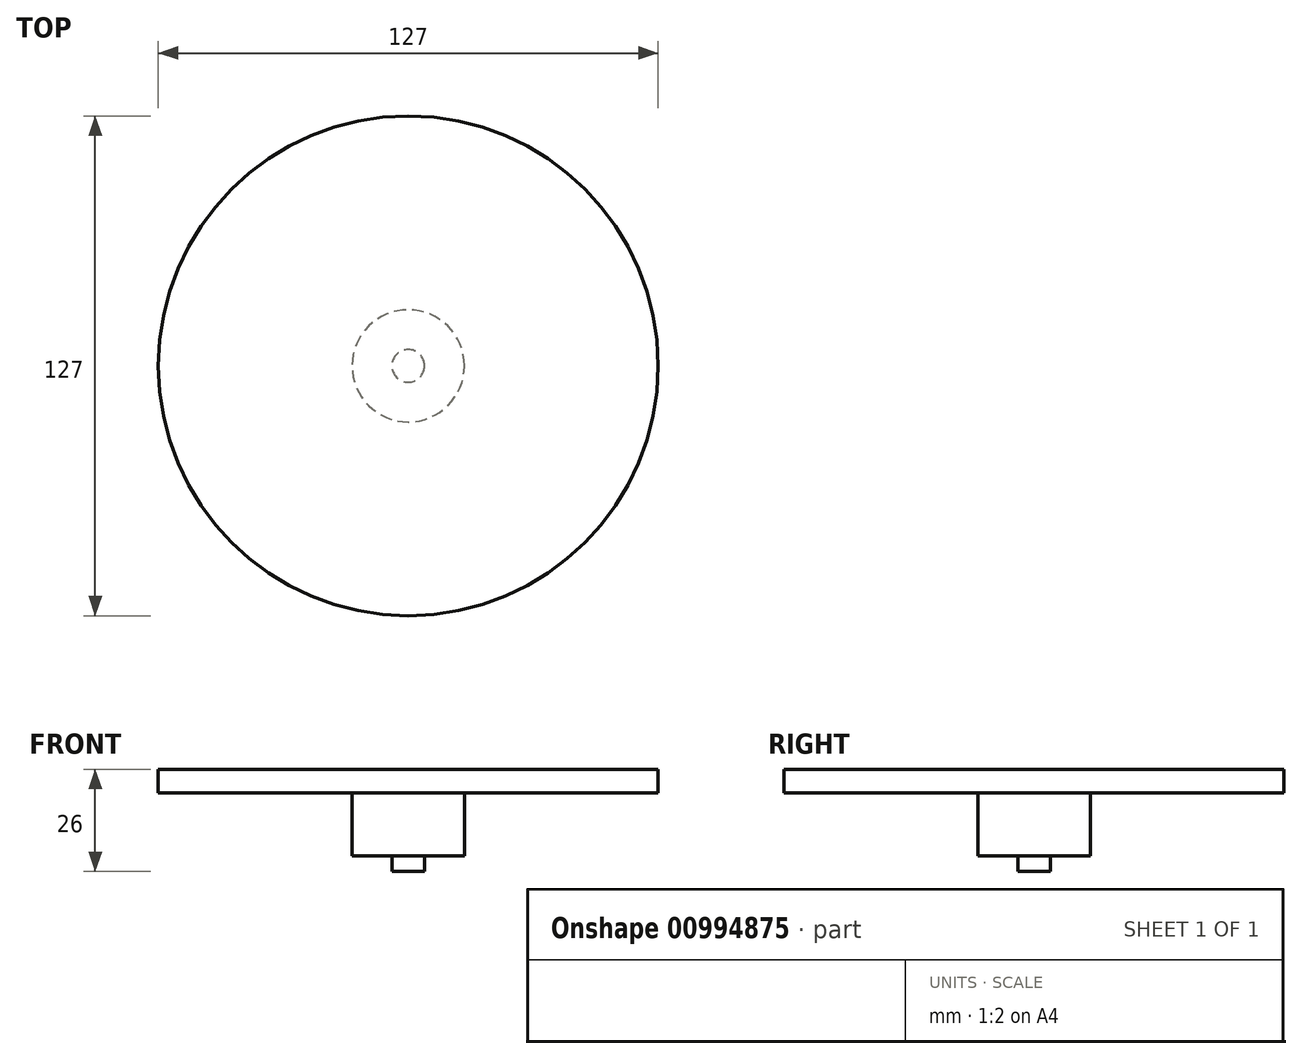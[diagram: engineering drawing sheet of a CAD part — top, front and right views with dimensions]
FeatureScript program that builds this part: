
annotation { "Feature Type Name" : "Feature", "Feature Type Description" : "" }
export const myFeature = defineFeature(function(context is Context, id is Id, definition is map)
    precondition{}
    {
        {
            var Q0;
            Q0=qCreatedBy(makeId("Top.planeOp"),FACE);
            var sketch = newSketch(context, id + "F0", { "sketchPlane" : qUnion([Q0])});
            skCircle(sketch, "E0", {"center": v(0, 0) * mm, "radius": 14.25 * mm});
            skCircle(sketch, "E1", {"center": v(0, 0) * mm, "radius": 2.5 * mm});
            skSolve(sketch);
        }
        {
            var Q0;
            Q0=makeQuery(id+"F0.imprint","IMPRINT",FACE,{"disambiguationData":[TD([[makeQuery(id+"F0.imprint","IMPRINT",EDGE,{"derivedFrom":sQuery(id+"F0.wireOp",EDGE,"E0")}),1.0]])]});
            extrude(context, id + "F1", {"entities" : qUnion([Q0]), "depth" : 16 * mm, "offsetDistance" : 25 * mm});
        }
        {
            var Q0;
            Q0=makeQuery(id+"F0.imprint","IMPRINT",FACE,{"disambiguationData":[TD([[makeQuery(id+"F0.imprint","IMPRINT",EDGE,{"derivedFrom":sQuery(id+"F0.wireOp",EDGE,"E1")}),1.0]])]});
            extrude(context, id + "F2", {"entities" : qUnion([Q0]), "operationType" : NewBodyOperationType.ADD, "depth" : 19 * mm, "offsetDistance" : 25 * mm});
        }
        {
            var Q0;
            Q0=makeQuery(id+"F1.opExtrude","CAP_FACE",FACE,{"disambiguationData":[OSD([sQuery(id+"F0.wireOp",EDGE,"E0"),sQuery(id+"F0.wireOp",EDGE,"E1")])],"isStart":false});
            var sketch = newSketch(context, id + "F3", { "sketchPlane" : qUnion([Q0])});
            skCircle(sketch, "E2", {"center": v(0, 0) * mm, "radius": 63.5 * mm});
            skSolve(sketch);
        }
        {
            var Q0;
            Q0=qSketchRegion(id+"F3",true);
            extrude(context, id + "F4", {"entities" : qUnion([Q0]), "operationType" : NewBodyOperationType.ADD, "depth" : 6 * mm, "offsetDistance" : 25 * mm});
        }
        {
            var Q0;
            {var subQ0=sQuery(id+"F0.wireOp",EDGE,"E1");Q0=makeQuery(id+"F2.boolean.opBoolean","MERGE",FACE,{"derivedFrom":[makeQuery(id+"F1.opExtrude","CAP_FACE",FACE,{"disambiguationData":[OSD([sQuery(id+"F0.wireOp",EDGE,"E0"),subQ0])],"isStart":true}),makeQuery(id+"F2.opExtrude","CAP_FACE",FACE,{"disambiguationData":[OSD([subQ0])],"isStart":true})]});}
            var sketch = newSketch(context, id + "F5", { "sketchPlane" : qUnion([Q0])});
            skCircle(sketch, "E3", {"center": v(0, 0) * mm, "radius": 4.15 * mm});
            skSolve(sketch);
        }
        {
            var Q0;
            Q0=qSketchRegion(id+"F5",true);
            extrude(context, id + "F6", {"entities" : qUnion([Q0]), "operationType" : NewBodyOperationType.ADD, "depth" : 4 * mm, "offsetDistance" : 25 * mm});
        }
    });
